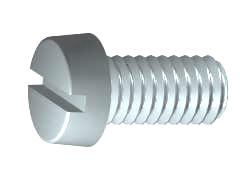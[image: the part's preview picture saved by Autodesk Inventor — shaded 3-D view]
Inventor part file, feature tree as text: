
AUTODESK INVENTOR PART (.ipt)
format: ipt  version: unknown  size: 279,040 bytes
history: native  units: mm (DEFAULTED — no unit token found)
features: other x1, extrude x1, plane x1
ambient origin geometry x7: Origin, YZ Plane, XZ Plane, X Axis, Y Axis, Z Axis, Center Point
feature tree (3):
  other  "Körper"
  extrude  "Loch"  Depth=10.0mm
  plane  "Work Plane1"
